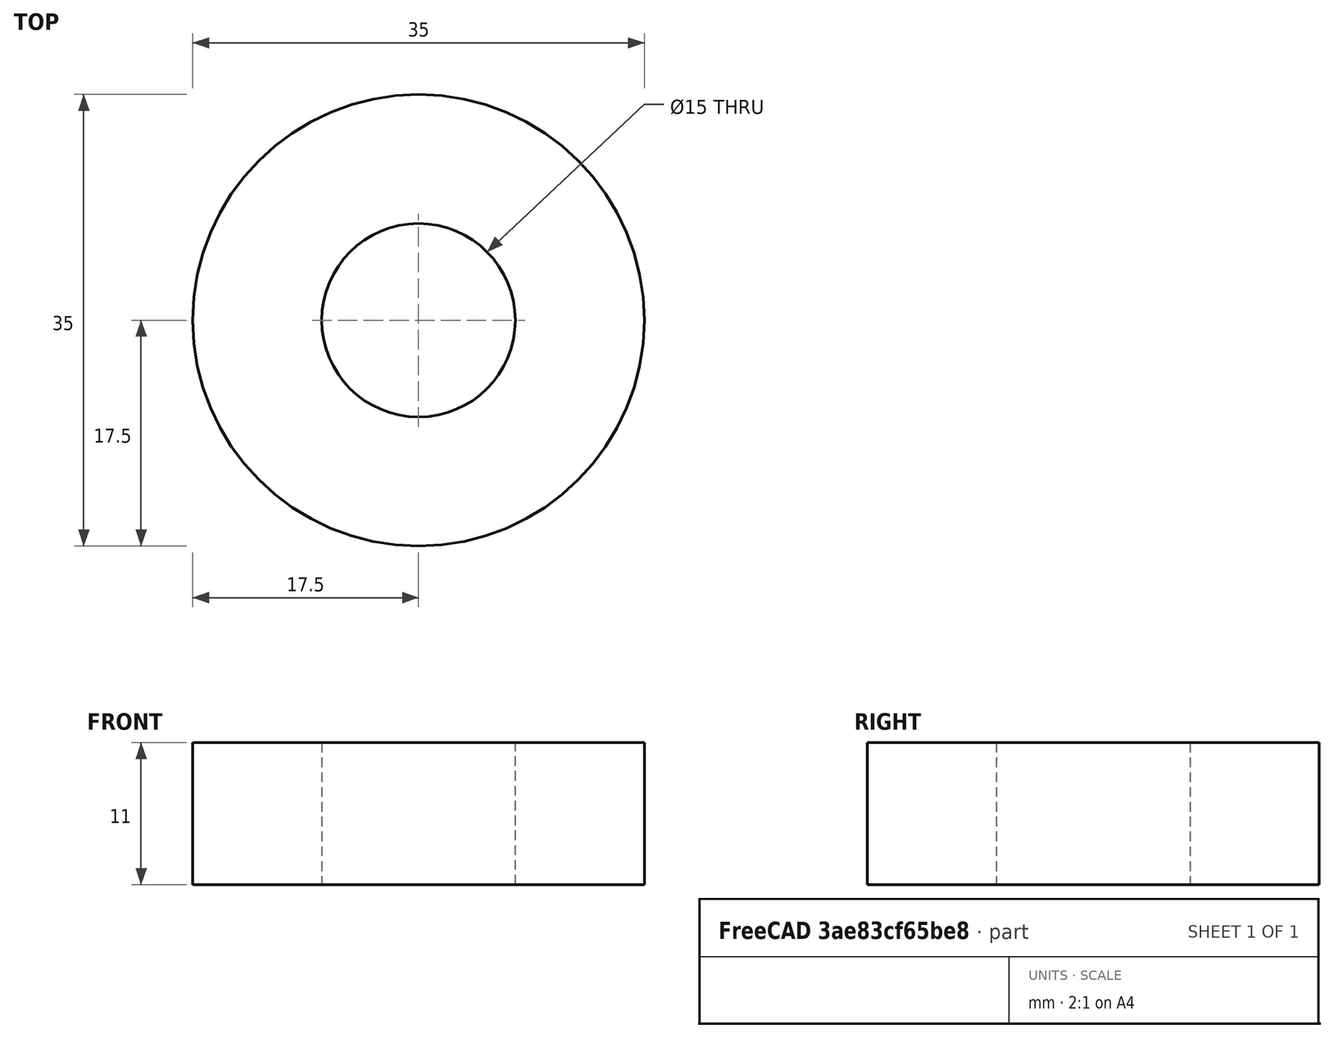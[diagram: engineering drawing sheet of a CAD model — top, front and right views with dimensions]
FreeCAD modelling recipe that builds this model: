
FCSTD DOCUMENT  (FreeCAD 1.0R39319 (Git))
Label: roulement
License: All rights reserved
LicenseURL: https://en.wikipedia.org/wiki/All_rights_reserved
objects: Sketcher::SketchObject×1, PartDesign::Pad×1, PartDesign::Body×1
note: 6 computed .brp shape members not serialized (recipe doc carries the construction recipe); baked Part::Feature solids carry a one-line shape summary decoded from their .brp

FEATURE [Sketcher::SketchObject] Sketch
  ArcFitTolerance = 1e-06
  AttachmentSupport = -> [XY_Plane]
  FullyConstrained = true
  MakeInternals = false
  MapMode = 5
  sketch-geometry (2):
    g0: Circle CenterX=0 CenterY=0 CenterZ=0 NormalX=0 NormalY=0 NormalZ=1 AngleXU=0 Radius=17.5
    g1: Circle CenterX=0 CenterY=0 CenterZ=0 NormalX=0 NormalY=0 NormalZ=1 AngleXU=0 Radius=7.5
  constraints (4):
    c: Coincident(g0,g-1)
    c: Coincident(g1,g0)
    c: Diameter(g1) = 15
    c: Diameter(g0) = 35
FEATURE [PartDesign::Pad] Pad
  Direction = (0,0,1)
  Length = 11
  Length2 = 10
  Profile = -> Sketch
  ReferenceAxis = -> Sketch [N_Axis]
  Refine = true
  Suppressed = false
  Type = 0
FEATURE [PartDesign::Body] Body  label="Corps"
  AllowCompound = false
  Group = -> [Sketch,Pad]
  Origin = -> Origin
  Tip = -> Pad
